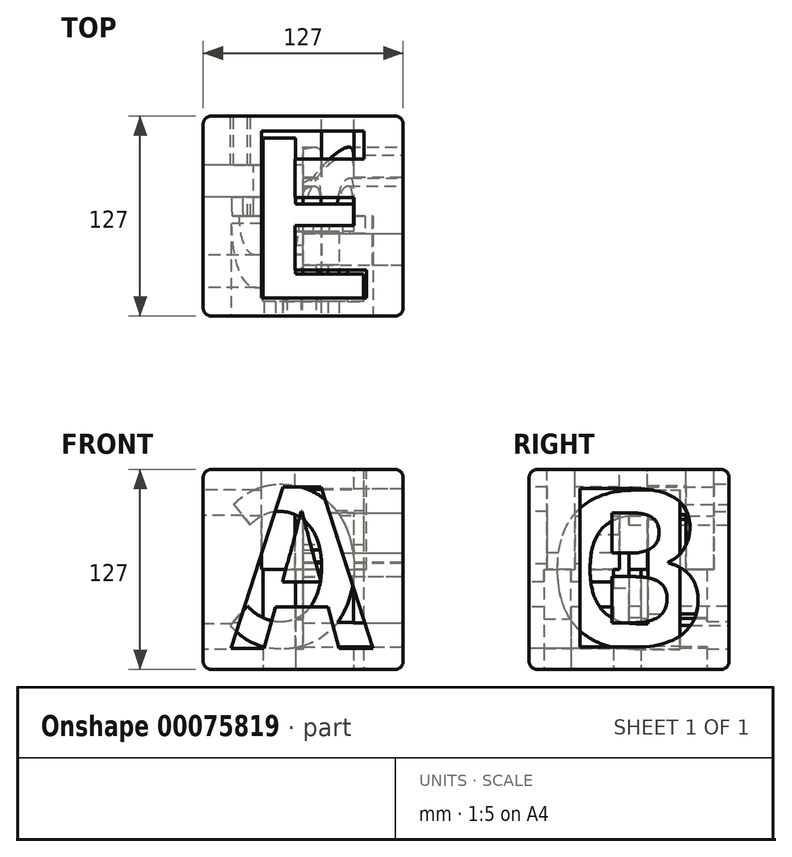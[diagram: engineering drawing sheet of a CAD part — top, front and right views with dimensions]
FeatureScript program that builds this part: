
annotation { "Feature Type Name" : "Feature", "Feature Type Description" : "" }
export const myFeature = defineFeature(function(context is Context, id is Id, definition is map)
    precondition{}
    {
        {
            var Q0;
            Q0=qCreatedBy(makeId("Top.planeOp"),FACE);
            var sketch = newSketch(context, id + "F0", { "sketchPlane" : qUnion([Q0])});
            skLineSegment(sketch, "E0.bottom", {"start": v(-63.5, 63.5) * mm, "end": v(63.5, 63.5) * mm});
            skLineSegment(sketch, "E0.top", {"start": v(-63.5, -63.5) * mm, "end": v(63.5, -63.5) * mm});
            skLineSegment(sketch, "E0.left", {"start": v(-63.5, 63.5) * mm, "end": v(-63.5, -63.5) * mm});
            skLineSegment(sketch, "E0.right", {"start": v(63.5, 63.5) * mm, "end": v(63.5, -63.5) * mm});
            skPoint(sketch, "E0.middle", {"position": v(0, 0) * mm});
            skSolve(sketch);
        }
        {
            var Q0;
            Q0 = qSketchRegion(id + "F0", true);
            extrude(context, id + "F1", {"entities" : qUnion([Q0]), "oppositeDirection" : true, "depth" : 63.5 * mm});
        }
        {
            var Q0;
            Q0=makeQuery(id+"F1.opExtrude","CAP_FACE",FACE,{"disambiguationData":[OSD([sQuery(id+"F0.wireOp",EDGE,"E0.bottom"),sQuery(id+"F0.wireOp",EDGE,"E0.top"),sQuery(id+"F0.wireOp",EDGE,"E0.left"),sQuery(id+"F0.wireOp",EDGE,"E0.right")])],"isStart":true});
            extrude(context, id + "F2", {"entities" : qUnion([Q0]), "operationType" : NewBodyOperationType.ADD, "depth" : 63.5 * mm});
        }
        {
            var Q0;
            {var subQ0=sQuery(id+"F0.wireOp",EDGE,"E0.top");Q0=makeQuery(id+"F2.boolean.opBoolean","MERGE",FACE,{"derivedFrom":[makeQuery(id+"F1.opExtrude","SWEPT_FACE",FACE,{"disambiguationData":[OSD([subQ0])]}),makeQuery(id+"F2.opExtrude","SWEPT_FACE",FACE,{"disambiguationData":[OSD([subQ0])]})]});}
            var sketch = newSketch(context, id + "F3", { "sketchPlane" : qUnion([Q0])});
            skText(sketch, "E1", { "text": "A", "fontName": "NotoSansCJKtc-Bold.otf"});
            const initialGuessF3  = {"E1": [-0.04522, -0.05026, 1, 0, 0.10004]};
            skSetInitialGuess(sketch, initialGuessF3);
            skSolve(sketch);
        }
        {
            var Q0;
            Q0 = qSketchRegion(id + "F3", true);
            extrude(context, id + "F4", {"entities" : qUnion([Q0]), "operationType" : NewBodyOperationType.REMOVE, "oppositeDirection" : true, "depth" : 63.5 * mm});
        }
        {
            var Q0;
            {var subQ0=sQuery(id+"F0.wireOp",EDGE,"E0.right");Q0=makeQuery(id+"F2.boolean.opBoolean","MERGE",FACE,{"derivedFrom":[makeQuery(id+"F1.opExtrude","SWEPT_FACE",FACE,{"disambiguationData":[OSD([subQ0])]}),makeQuery(id+"F2.opExtrude","SWEPT_FACE",FACE,{"disambiguationData":[OSD([subQ0])]})]});}
            var sketch = newSketch(context, id + "F5", { "sketchPlane" : qUnion([Q0])});
            skText(sketch, "E2", { "text": "B", "fontName": "NotoSansCJKtc-Bold.otf"});
            const initialGuessF5  = {"E2": [-0.04358, -0.04932, 1, 0, 0.09793]};
            skSetInitialGuess(sketch, initialGuessF5);
            skSolve(sketch);
        }
        {
            var Q0;
            Q0 = qSketchRegion(id + "F5", true);
            extrude(context, id + "F6", {"entities" : qUnion([Q0]), "operationType" : NewBodyOperationType.REMOVE, "oppositeDirection" : true, "depth" : 63.5 * mm});
        }
        {
            var Q0;
            {var subQ0=sQuery(id+"F0.wireOp",EDGE,"E0.bottom");Q0=makeQuery(id+"F2.boolean.opBoolean","MERGE",FACE,{"derivedFrom":[makeQuery(id+"F1.opExtrude","SWEPT_FACE",FACE,{"disambiguationData":[OSD([subQ0])]}),makeQuery(id+"F2.opExtrude","SWEPT_FACE",FACE,{"disambiguationData":[OSD([subQ0])]})]});}
            var sketch = newSketch(context, id + "F7", { "sketchPlane" : qUnion([Q0])});
            skText(sketch, "E3", { "text": "C", "fontName": "NotoSansCJKtc-Bold.otf"});
            const initialGuessF7  = {"E3": [-0.0396, -0.04862, 1, 0, 0.09817]};
            skSetInitialGuess(sketch, initialGuessF7);
            skSolve(sketch);
        }
        {
            var Q0;
            Q0 = qSketchRegion(id + "F7", true);
            extrude(context, id + "F8", {"entities" : qUnion([Q0]), "operationType" : NewBodyOperationType.REMOVE, "oppositeDirection" : true, "depth" : 63.5 * mm});
        }
        {
            var Q0;
            {var subQ0=sQuery(id+"F0.wireOp",EDGE,"E0.left");Q0=makeQuery(id+"F2.boolean.opBoolean","MERGE",FACE,{"derivedFrom":[makeQuery(id+"F1.opExtrude","SWEPT_FACE",FACE,{"disambiguationData":[OSD([subQ0])]}),makeQuery(id+"F2.opExtrude","SWEPT_FACE",FACE,{"disambiguationData":[OSD([subQ0])]})]});}
            var sketch = newSketch(context, id + "F9", { "sketchPlane" : qUnion([Q0])});
            skText(sketch, "E4", { "text": "D", "fontName": "NotoSansCJKtc-Bold.otf"});
            const initialGuessF9  = {"E4": [-0.04475, -0.05072, 1, 0, 0.0984]};
            skSetInitialGuess(sketch, initialGuessF9);
            skSolve(sketch);
        }
        {
            var Q0;
            Q0 = qSketchRegion(id + "F9", true);
            extrude(context, id + "F10", {"entities" : qUnion([Q0]), "operationType" : NewBodyOperationType.REMOVE, "oppositeDirection" : true, "depth" : 63.5 * mm});
        }
        {
            var Q0;
            Q0=makeQuery(id+"F2.opExtrude","CAP_FACE",FACE,{"disambiguationData":[OSD([sQuery(id+"F0.wireOp",EDGE,"E0.bottom"),sQuery(id+"F0.wireOp",EDGE,"E0.top"),sQuery(id+"F0.wireOp",EDGE,"E0.left"),sQuery(id+"F0.wireOp",EDGE,"E0.right")])],"isStart":false});
            var sketch = newSketch(context, id + "F11", { "sketchPlane" : qUnion([Q0])});
            skText(sketch, "E5", { "text": "E", "fontName": "NotoSansCJKtc-Bold.otf"});
            const initialGuessF11  = {"E5": [-0.03936, -0.05213, 1, 0, 0.10309]};
            skSetInitialGuess(sketch, initialGuessF11);
            skSolve(sketch);
        }
        {
            var Q0;
            Q0 = qSketchRegion(id + "F11", true);
            extrude(context, id + "F12", {"entities" : qUnion([Q0]), "operationType" : NewBodyOperationType.REMOVE, "oppositeDirection" : true, "depth" : 63.5 * mm});
        }
        {
            var Q0;
            Q0=makeQuery(id+"F1.opExtrude","CAP_FACE",FACE,{"disambiguationData":[OSD([sQuery(id+"F0.wireOp",EDGE,"E0.bottom"),sQuery(id+"F0.wireOp",EDGE,"E0.top"),sQuery(id+"F0.wireOp",EDGE,"E0.left"),sQuery(id+"F0.wireOp",EDGE,"E0.right")])],"isStart":false});
            var sketch = newSketch(context, id + "F13", { "sketchPlane" : qUnion([Q0])});
            skText(sketch, "E6", { "text": "F", "fontName": "NotoSansCJKtc-Bold.otf"});
            const initialGuessF13  = {"E6": [-0.03842, -0.04955, 1, 0, 0.10098]};
            skSetInitialGuess(sketch, initialGuessF13);
            skSolve(sketch);
        }
        {
            var Q0;
            Q0 = qSketchRegion(id + "F13", true);
            extrude(context, id + "F14", {"entities" : qUnion([Q0]), "operationType" : NewBodyOperationType.REMOVE, "oppositeDirection" : true, "depth" : 63.5 * mm});
        }
        {
            var Q0;
            Q0=makeQuery(id+"F2.opExtrude","CAP_EDGE",EDGE,{"disambiguationData":[OSD([sQuery(id+"F0.wireOp",EDGE,"E0.top")])],"isStart":false});
            var Q1;
            Q1=makeQuery(id+"F2.opExtrude","CAP_EDGE",EDGE,{"disambiguationData":[OSD([sQuery(id+"F0.wireOp",EDGE,"E0.left")])],"isStart":false});
            var Q2;
            Q2=makeQuery(id+"F2.opExtrude","CAP_EDGE",EDGE,{"disambiguationData":[OSD([sQuery(id+"F0.wireOp",EDGE,"E0.right")])],"isStart":false});
            var Q3;
            Q3=makeQuery(id+"F2.opExtrude","CAP_EDGE",EDGE,{"disambiguationData":[OSD([sQuery(id+"F0.wireOp",EDGE,"E0.bottom")])],"isStart":false});
            var Q4;
            {var subQ0=sQuery(id+"F0.wireOp",EDGE,"E0.right");var subQ1=sQuery(id+"F0.wireOp",EDGE,"E0.top");Q4=makeQuery(id+"F2.boolean.opBoolean","MERGE",EDGE,{"derivedFrom":[makeQuery(id+"F1.opExtrude","SWEPT_EDGE",EDGE,{"disambiguationData":[OSD([subQ1,subQ0])]}),makeQuery(id+"F2.opExtrude","SWEPT_EDGE",EDGE,{"disambiguationData":[OSD([subQ1,subQ0])]})]});}
            var Q5;
            {var subQ0=sQuery(id+"F0.wireOp",EDGE,"E0.left");var subQ1=sQuery(id+"F0.wireOp",EDGE,"E0.top");Q5=makeQuery(id+"F2.boolean.opBoolean","MERGE",EDGE,{"derivedFrom":[makeQuery(id+"F1.opExtrude","SWEPT_EDGE",EDGE,{"disambiguationData":[OSD([subQ1,subQ0])]}),makeQuery(id+"F2.opExtrude","SWEPT_EDGE",EDGE,{"disambiguationData":[OSD([subQ1,subQ0])]})]});}
            var Q6;
            Q6=makeQuery(id+"F1.opExtrude","CAP_EDGE",EDGE,{"disambiguationData":[OSD([sQuery(id+"F0.wireOp",EDGE,"E0.top")])],"isStart":false});
            var Q7;
            Q7=makeQuery(id+"F1.opExtrude","CAP_EDGE",EDGE,{"disambiguationData":[OSD([sQuery(id+"F0.wireOp",EDGE,"E0.right")])],"isStart":false});
            var Q8;
            {var subQ0=sQuery(id+"F0.wireOp",EDGE,"E0.right");var subQ1=sQuery(id+"F0.wireOp",EDGE,"E0.bottom");Q8=makeQuery(id+"F2.boolean.opBoolean","MERGE",EDGE,{"derivedFrom":[makeQuery(id+"F1.opExtrude","SWEPT_EDGE",EDGE,{"disambiguationData":[OSD([subQ1,subQ0])]}),makeQuery(id+"F2.opExtrude","SWEPT_EDGE",EDGE,{"disambiguationData":[OSD([subQ1,subQ0])]})]});}
            var Q9;
            {var subQ0=sQuery(id+"F0.wireOp",EDGE,"E0.left");var subQ1=sQuery(id+"F0.wireOp",EDGE,"E0.bottom");Q9=makeQuery(id+"F2.boolean.opBoolean","MERGE",EDGE,{"derivedFrom":[makeQuery(id+"F1.opExtrude","SWEPT_EDGE",EDGE,{"disambiguationData":[OSD([subQ1,subQ0])]}),makeQuery(id+"F2.opExtrude","SWEPT_EDGE",EDGE,{"disambiguationData":[OSD([subQ1,subQ0])]})]});}
            var Q10;
            Q10=makeQuery(id+"F1.opExtrude","CAP_EDGE",EDGE,{"disambiguationData":[OSD([sQuery(id+"F0.wireOp",EDGE,"E0.bottom")])],"isStart":false});
            var Q11;
            Q11=makeQuery(id+"F1.opExtrude","CAP_EDGE",EDGE,{"disambiguationData":[OSD([sQuery(id+"F0.wireOp",EDGE,"E0.left")])],"isStart":false});
            fillet(context, id + "F15", {"entities" : qUnion([Q0, Q1, Q2, Q3, Q4, Q5, Q6, Q7, Q8, Q9, Q10, Q11]), "radius" : 5.08 * mm, "tangentPropagation" : true, "allowEdgeOverflow" : false});
        }
    });
